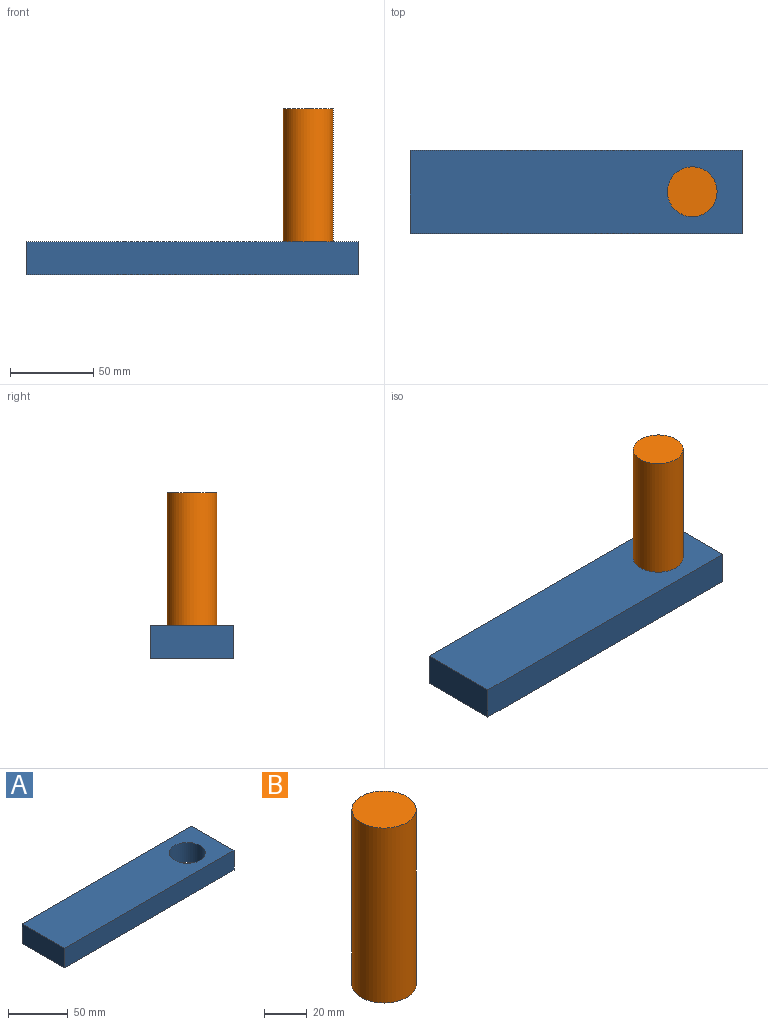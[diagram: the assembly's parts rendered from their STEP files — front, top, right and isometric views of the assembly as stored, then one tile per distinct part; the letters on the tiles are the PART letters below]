
ASSEMBLY  parts=2 mates=1
PART A: 7 faces, bbox 200x50x20 mm
  f0: plane 200x20mm, normal (0,1,0), area 4000mm2, adj f1,f3,f4,f5
  f1: plane 50x20mm, normal (-1,0,0), area 1000mm2, adj f0,f2,f4,f5
  f2: plane 200x20mm, normal (0,-1,0), area 4000mm2, adj f1,f3,f4,f5
  f3: plane 50x20mm, normal (1,0,0), area 1000mm2, adj f0,f2,f4,f5
  f4: plane 200x50mm, normal (0,0,1), area 9293.1mm2, adj f0,f1,f2,f3,f6
  f5: plane 200x50mm, normal (0,0,-1), area 9293.1mm2, adj f0,f1,f2,f3,f6
  f6: cylinder r=15mm len=30mm, axis (0,0,1), area 1885mm2, adj f4,f5
PART B: 3 faces, bbox 30x30x100 mm
  f0: cylinder r=15mm len=100mm, axis (0,0,-1), area 9424.8mm2, adj f1,f2
  f1: plane 30x30mm, normal (0,0,1), area 706.9mm2, adj f0
  f2: plane 30x30mm, normal (0,0,-1), area 706.9mm2, adj f0
PLACE A t=(-126.91,-56.96,-25.53)mm fixed
PLACE B t=(-62.32,-58.24,-25.53)mm
MATE slider B.f0 <-> A.f6  axis (0,0,-1) through (-62.32,-58.24,-25.53)mm
